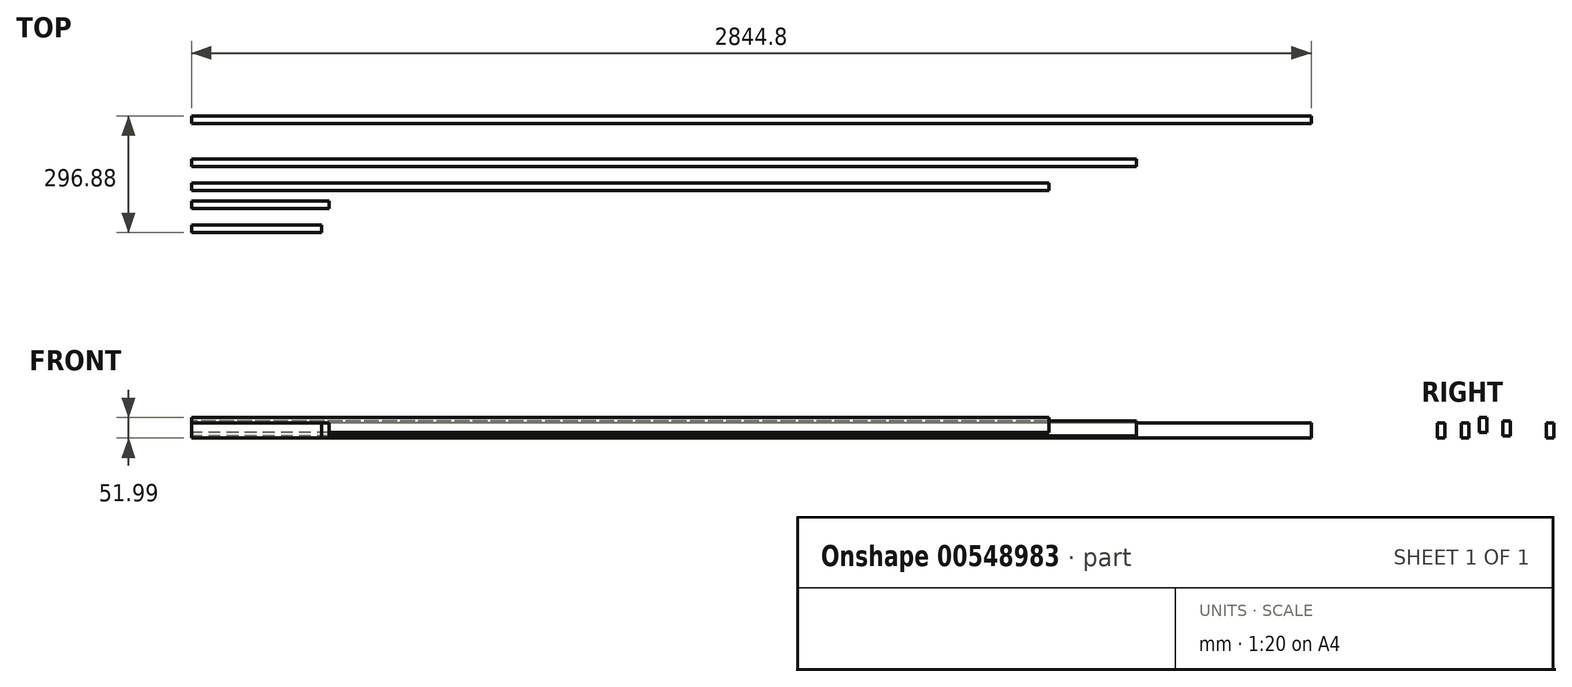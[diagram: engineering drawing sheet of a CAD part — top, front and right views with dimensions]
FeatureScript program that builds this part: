
annotation { "Feature Type Name" : "Feature", "Feature Type Description" : "" }
export const myFeature = defineFeature(function(context is Context, id is Id, definition is map)
    precondition{}
    {
        {
            var Q0;
            Q0=qCreatedBy(makeId("Right.planeOp"),FACE);
            var sketch = newSketch(context, id + "F0", { "sketchPlane" : qUnion([Q0])});
            skLineSegment(sketch, "E0.bottom", {"start": v(9.53, 19.05) * mm, "end": v(-9.52, 19.05) * mm});
            skLineSegment(sketch, "E0.top", {"start": v(9.53, -19.05) * mm, "end": v(-9.52, -19.05) * mm});
            skLineSegment(sketch, "E0.left", {"start": v(9.53, 19.05) * mm, "end": v(9.53, -19.05) * mm});
            skLineSegment(sketch, "E0.right", {"start": v(-9.52, 19.05) * mm, "end": v(-9.52, -19.05) * mm});
            skPoint(sketch, "E0.middle", {"position": v(0, 0) * mm});
            skLineSegment(sketch, "E1.top", {"start": v(9.53, -19.05) * mm, "end": v(-9.53, -19.05) * mm});
            skLineSegment(sketch, "E1.right", {"start": v(-9.52, 19.05) * mm, "end": v(-9.53, -19.05) * mm});
            skSolve(sketch);
        }
        {
            var Q0;
            Q0=makeQuery(id+"F0.imprint","IMPRINT",FACE,{"disambiguationData":[TD([[makeQuery(id+"F0.imprint","IMPRINT",EDGE,{"derivedFrom":sQuery(id+"F0.wireOp",EDGE,"E0.bottom")}),1.0]])]});
            extrude(context, id + "F1", {"entities" : qUnion([Q0]), "depth" : 349.25 * mm, "offsetDistance" : 25.4 * mm});
        }
        {
            var Q0;
            Q0=qCreatedBy(makeId("Right.planeOp"),FACE);
            var sketch = newSketch(context, id + "F2", { "sketchPlane" : qUnion([Q0])});
            skLineSegment(sketch, "E2.bottom", {"start": v(115.79, 25.12) * mm, "end": v(96.74, 25.12) * mm});
            skLineSegment(sketch, "E2.top", {"start": v(115.79, -12.98) * mm, "end": v(96.74, -12.98) * mm});
            skLineSegment(sketch, "E2.left", {"start": v(115.79, 25.12) * mm, "end": v(115.79, -12.98) * mm});
            skLineSegment(sketch, "E2.right", {"start": v(96.74, 25.12) * mm, "end": v(96.74, -12.98) * mm});
            skPoint(sketch, "E2.middle", {"position": v(106.26, 6.07) * mm});
            skSolve(sketch);
        }
        {
            var Q0;
            Q0=makeQuery(id+"F2.imprint","IMPRINT",FACE,{"disambiguationData":[TD([[makeQuery(id+"F2.imprint","IMPRINT",EDGE,{"derivedFrom":sQuery(id+"F2.wireOp",EDGE,"E2.bottom")}),1.0]])]});
            extrude(context, id + "F3", {"entities" : qUnion([Q0]), "depth" : 2400.3 * mm, "offsetDistance" : 25.4 * mm});
        }
        {
            var Q0;
            Q0=qCreatedBy(makeId("Right.planeOp"),FACE);
            var sketch = newSketch(context, id + "F4", { "sketchPlane" : qUnion([Q0])});
            skLineSegment(sketch, "E3.bottom", {"start": v(226.24, 19.66) * mm, "end": v(207.2, 19.66) * mm});
            skLineSegment(sketch, "E3.top", {"start": v(226.24, -18.44) * mm, "end": v(207.2, -18.44) * mm});
            skLineSegment(sketch, "E3.left", {"start": v(226.24, 19.66) * mm, "end": v(226.24, -18.44) * mm});
            skLineSegment(sketch, "E3.right", {"start": v(207.2, 19.66) * mm, "end": v(207.2, -18.44) * mm});
            skPoint(sketch, "E3.middle", {"position": v(216.72, 0.6) * mm});
            skSolve(sketch);
        }
        {
            var Q0;
            Q0=makeQuery(id+"F4.imprint","IMPRINT",FACE,{"disambiguationData":[TD([[makeQuery(id+"F4.imprint","IMPRINT",EDGE,{"derivedFrom":sQuery(id+"F4.wireOp",EDGE,"E3.bottom")}),1.0]])]});
            extrude(context, id + "F5", {"entities" : qUnion([Q0]), "depth" : 2844.8 * mm, "offsetDistance" : 25.4 * mm});
        }
        {
            var Q0;
            Q0=qCreatedBy(makeId("Right.planeOp"),FACE);
            var sketch = newSketch(context, id + "F6", { "sketchPlane" : qUnion([Q0])});
            skLineSegment(sketch, "E4.bottom", {"start": v(55.84, 32.94) * mm, "end": v(36.79, 32.94) * mm});
            skLineSegment(sketch, "E4.top", {"start": v(55.84, -5.16) * mm, "end": v(36.79, -5.16) * mm});
            skLineSegment(sketch, "E4.left", {"start": v(55.84, 32.94) * mm, "end": v(55.84, -5.16) * mm});
            skLineSegment(sketch, "E4.right", {"start": v(36.79, 32.94) * mm, "end": v(36.79, -5.16) * mm});
            skPoint(sketch, "E4.middle", {"position": v(46.31, 13.89) * mm});
            skSolve(sketch);
        }
        {
            var Q0;
            Q0=makeQuery(id+"F6.imprint","IMPRINT",FACE,{"disambiguationData":[TD([[makeQuery(id+"F6.imprint","IMPRINT",EDGE,{"derivedFrom":sQuery(id+"F6.wireOp",EDGE,"E4.bottom")}),1.0]])]});
            extrude(context, id + "F7", {"entities" : qUnion([Q0]), "depth" : 2178.05 * mm, "offsetDistance" : 25.4 * mm});
        }
        {
            var Q0;
            Q0=qCreatedBy(makeId("Right.planeOp"),FACE);
            var sketch = newSketch(context, id + "F8", { "sketchPlane" : qUnion([Q0])});
            skLineSegment(sketch, "E5.bottom", {"start": v(-51.6, 19.05) * mm, "end": v(-70.64, 19.05) * mm});
            skLineSegment(sketch, "E5.top", {"start": v(-51.6, -19.05) * mm, "end": v(-70.64, -19.05) * mm});
            skLineSegment(sketch, "E5.left", {"start": v(-51.6, 19.05) * mm, "end": v(-51.6, -19.05) * mm});
            skLineSegment(sketch, "E5.right", {"start": v(-70.64, 19.05) * mm, "end": v(-70.64, -19.05) * mm});
            skPoint(sketch, "E5.middle", {"position": v(-61.12, 0) * mm});
            skSolve(sketch);
        }
        {
            var Q0;
            Q0=makeQuery(id+"F8.imprint","IMPRINT",FACE,{"disambiguationData":[TD([[makeQuery(id+"F8.imprint","IMPRINT",EDGE,{"derivedFrom":sQuery(id+"F8.wireOp",EDGE,"E5.bottom")}),1.0]])]});
            extrude(context, id + "F9", {"entities" : qUnion([Q0]), "depth" : 330.2 * mm, "offsetDistance" : 25.4 * mm});
        }
    });
